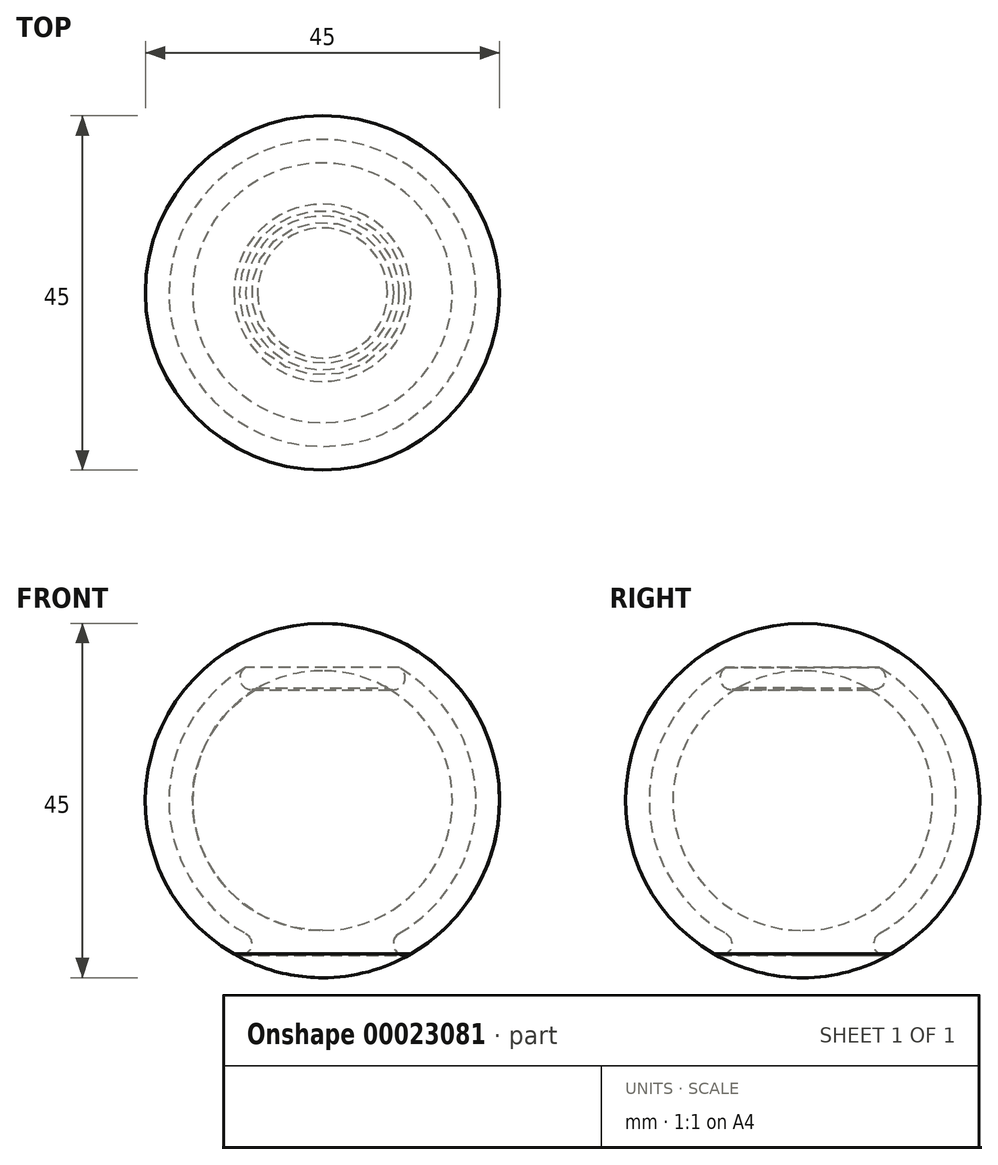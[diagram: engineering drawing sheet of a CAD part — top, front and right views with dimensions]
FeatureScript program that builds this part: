
annotation { "Feature Type Name" : "Feature", "Feature Type Description" : "" }
export const myFeature = defineFeature(function(context is Context, id is Id, definition is map)
    precondition{}
    {
        {
            var Q0;
            Q0=qCreatedBy(makeId("Front.planeOp"),FACE);
            var sketch = newSketch(context, id + "F0", { "sketchPlane" : qUnion([Q0])});
            skCircle(sketch, "E0", {"center": v(0, 0) * mm, "radius": 22.5 * mm, "construction": true});
            skArc(sketch, "E1", {"start": v(-9.75, 16.89) * mm, "mid": v(-18.84, -5.05) * mm, "end": v(0, -19.5) * mm});
            skLineSegment(sketch, "E2", {"start": v(0, 0) * mm, "end": v(-11.25, -19.49) * mm, "construction": true});
            skArc(sketch, "E3", {"start": v(-11.25, -19.49) * mm, "mid": v(-9.2, -18.94) * mm, "end": v(-9.75, -16.89) * mm});
            skArc(sketch, "E4", {"start": v(-11.25, -19.49) * mm, "mid": v(-5.82, -21.73) * mm, "end": v(0, -22.5) * mm});
            skArc(sketch, "E5", {"start": v(-8.25, 14.29) * mm, "mid": v(-15.94, -4.27) * mm, "end": v(0, -16.5) * mm});
            skPoint(sketch, "E6", {"position": v(0, -22.5) * mm});
            skPoint(sketch, "E7", {"position": v(0, -19.5) * mm});
            skPoint(sketch, "E8", {"position": v(0, -16.5) * mm});
            skLineSegment(sketch, "E9", {"start": v(0, 0) * mm, "end": v(-9.75, 16.89) * mm, "construction": true});
            skArc(sketch, "E10", {"start": v(-9.75, 16.89) * mm, "mid": v(-10.3, 14.84) * mm, "end": v(-8.25, 14.29) * mm});
            skLineSegment(sketch, "E11", {"start": v(0, 42.1) * mm, "end": v(0, -44) * mm, "construction": true});
            skPoint(sketch, "E12.end.orphan", {"position": v(11.25, -19.49) * mm});
            skLineSegment(sketch, "E13", {"start": v(0, -16.5) * mm, "end": v(0, -22.5) * mm});
            skLineSegment(sketch, "E14", {"start": v(0, -19.5) * mm, "end": v(0, -22.5) * mm});
            skLineSegment(sketch, "E15", {"start": v(0, -16.5) * mm, "end": v(0, -19.5) * mm});
            skArc(sketch, "E16", {"start": v(0, 16.5) * mm, "mid": v(-4.27, 15.94) * mm, "end": v(-8.25, 14.29) * mm});
            skLineSegment(sketch, "E17", {"start": v(0, 16.5) * mm, "end": v(0, 22.5) * mm});
            skArc(sketch, "E18", {"start": v(0, 22.5) * mm, "mid": v(-21.73, 5.82) * mm, "end": v(-11.25, -19.49) * mm});
            skSolve(sketch);
        }
        {
            var Q0;
            {var subQ1=sQuery(id+"F0.wireOp",EDGE,"E5");Q0=makeQuery(id+"F0.imprint","IMPRINT",FACE,{"disambiguationData":[TD([[makeQuery(id+"F0.imprint","IMPRINT",EDGE,{"derivedFrom":subQ1}),-1.0]])]});}
            var Q1;
            {var subQ4=sQuery(id+"F0.wireOp",EDGE,"E3");Q1=makeQuery(id+"F0.imprint","IMPRINT",FACE,{"disambiguationData":[TD([[makeQuery(id+"F0.imprint","IMPRINT",EDGE,{"derivedFrom":subQ4}),-1.0]])]});}
            var Q2;
            Q2=sQuery(id+"F0.wireOp",EDGE,"E11");
            revolve(context, id + "F1", {"entities" : qUnion([Q0, Q1]), "axis" : qUnion([Q2]), "revolveType" : RevolveType.FULL});
        }
        {
            var Q0;
            {var subQ1=sQuery(id+"F0.wireOp",EDGE,"E3");Q0=makeQuery(id+"F0.imprint","IMPRINT",FACE,{"disambiguationData":[TD([[makeQuery(id+"F0.imprint","IMPRINT",EDGE,{"derivedFrom":subQ1}),1.0]])]});}
            var Q1;
            Q1=sQuery(id+"F0.wireOp",EDGE,"E11");
            revolve(context, id + "F2", {"entities" : qUnion([Q0]), "axis" : qUnion([Q1]), "revolveType" : RevolveType.FULL});
        }
    });
